# Revit family: NBS_PineappleContracts_OffcTbl_RynoCoffeeTable
name_source: partatom
category: Furniture
revit_build: Autodesk Revit 2017 (Build: 20171027_0315(x64)
units: mm (PartAtom-declared; Revit-internal decimal feet)

## family parameters
Always vertical = Yes
Cut with Voids When Loaded = No
Room Calculation Point = No
Shared = No
Work Plane-Based = No

## types (1)
- NBS_PineappleContracts_OfficeTables_RynoCoffeeTable
    AssetType = Movable
    BIMObjectName = NBS_PineappleContracts_OfficeTables_RynoCoffeeTable
    Category = Pr_40_50_21_60:Office tables
    ColourOptions = Black, Dark blue, Granite, Light blue, Lime, Orange, Red, White
    Description = Polyethylene coffee table
    DurationUnit = year
    ExposedEdges = Rounded
    Feet = Stainless steel glides
    Finish = Anti-microbial, wipe-clean surface with excellent chemical resistance
    FrameSupports = Contoured table design
    Functions = Lounge
    IfcExportAs = IfcFurnishingElementType
    IfcExportType = TABLE
    IsBuiltIn = No
    Manufacturer = www.pineapplecontracts.com
    ManufacturerName = Pineapple Contracts
    ManufacturerURL = www.pineapplecontracts.com
    Material = Polyethylene
    ModelNumber = ARYF-002
    ModelReference = Ryno Coffee Table
    NBSCertification = www.nationalbimlibrary.com/cert/0b1bunc4
    NBSDescription = Office tables
    NBSReference = 45-35-20/340
    Name = OfficeTables_RynoCoffeeTable_PineappleContracts
    NominalDepth = 0 mm  [stored 0 ft]
    NominalHeight = 425 mm  [stored 1.39436 ft]
    NominalLength = 655 mm  [stored 2.14895 ft]
    NominalWidth = 655 mm  [stored 2.14895 ft]
    NumberOfChairs = 0
    ProductInformation = www.pineapplecontracts.com/userfiles/file/RYNO-brochure.pdf
    Shape = Square
    Size = 655 x 655 x 425 mm
    StrengthAndStability = Level 3
    TableMaterial = NBS_Concept
    TableTop = Flat laminate
    Uniclass2015Code = Pr_40_50_21_60
    Uniclass2015Title = Office tables
    Uniclass2015Version = Products v1.5
    Version = 6
    WallThickness = 0 mm  [stored 0 ft]
    WarrantyDescription = Guarantee against manufacturing faults
    WarrantyDurationParts = 7
    WarrantyDurationUnit = year
    Weight = 50 kg
    WorksurfaceArea = 0 m²

note: [stored X ft] marks values corroborated as IEEE doubles in the binary element streams (Revit-internal decimal feet)

## geometry (parser evidence)
native form markers: Sweep x2
no freeform markers — native parametric forms only
